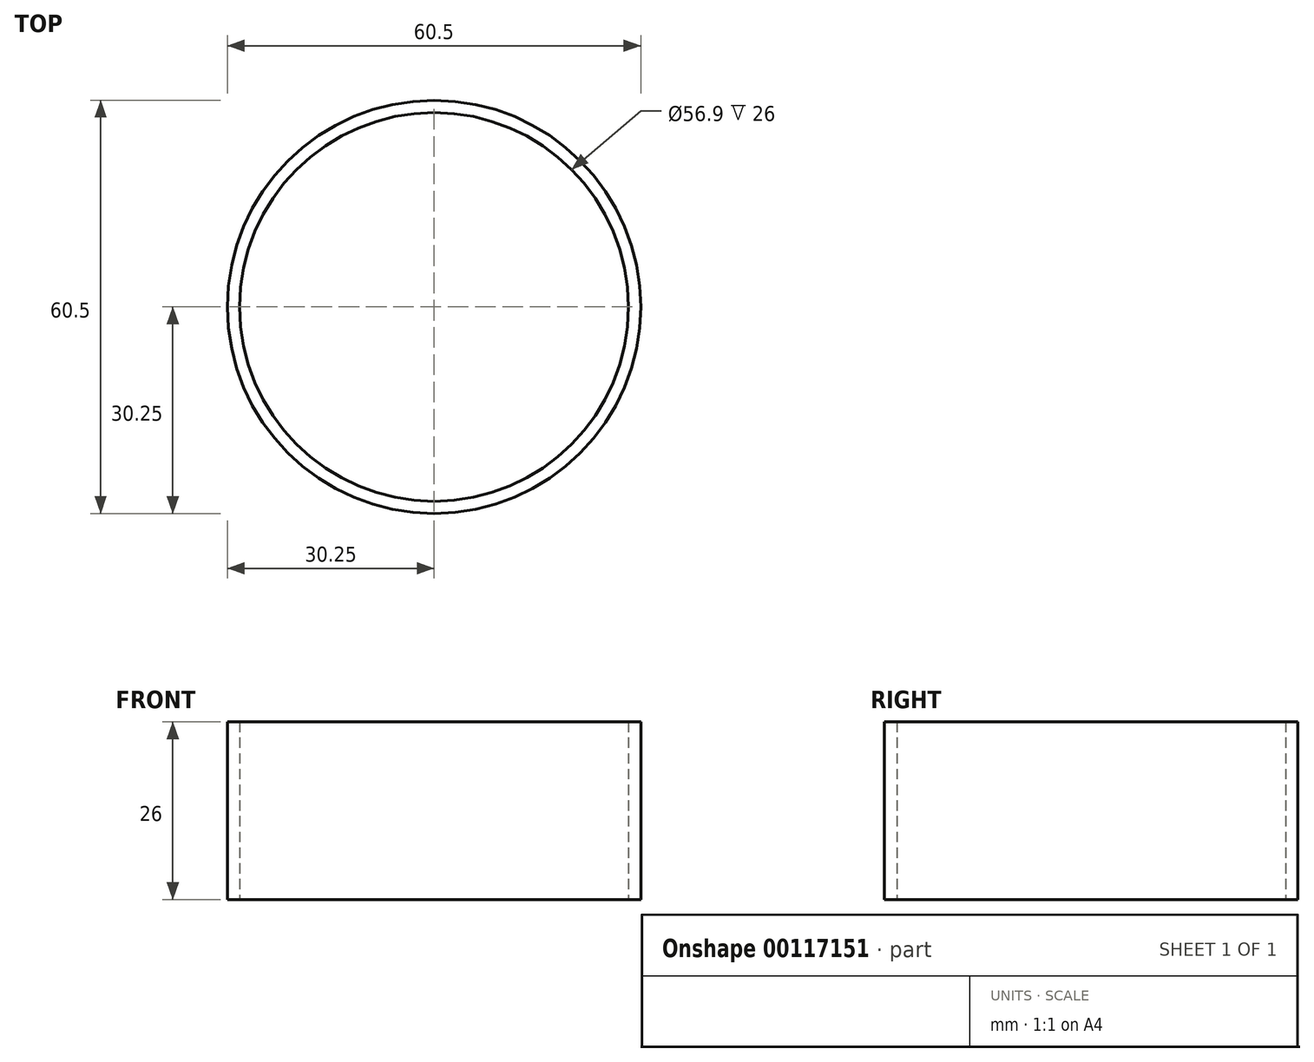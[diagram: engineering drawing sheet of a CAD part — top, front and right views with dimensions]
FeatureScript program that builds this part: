
annotation { "Feature Type Name" : "Feature", "Feature Type Description" : "" }
export const myFeature = defineFeature(function(context is Context, id is Id, definition is map)
    precondition{}
    {
        {
            var Q0;
            Q0=qCreatedBy(makeId("Top.planeOp"),FACE);
            var sketch = newSketch(context, id + "F0", { "sketchPlane" : qUnion([Q0])});
            skCircle(sketch, "E0", {"center": v(0, 0) * mm, "radius": 28.45 * mm});
            skCircle(sketch, "E1", {"center": v(0, 0) * mm, "radius": 30.25 * mm});
            skSolve(sketch);
        }
        {
            var Q0;
            Q0=makeQuery(id+"F0.imprint","IMPRINT",FACE,{"disambiguationData":[TD([[makeQuery(id+"F0.imprint","IMPRINT",EDGE,{"derivedFrom":sQuery(id+"F0.wireOp",EDGE,"E0")}),-1.0]])]});
            extrude(context, id + "F1", {"entities" : qUnion([Q0]), "depth" : 26 * mm});
        }
    });
